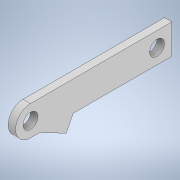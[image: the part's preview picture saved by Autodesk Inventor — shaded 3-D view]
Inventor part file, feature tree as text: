
AUTODESK INVENTOR PART (.ipt)
format: ipt  version: 2021 (Build 250183000, 183)  size: 136,192 bytes
history: native  units: in
note: dims shown in document units (in); Inventor stores cm internally (conversion verified against a paired STEP export)
features: extrude x4, sketch x4, projected_geometry x1
ambient origin geometry x8: Origin, YZ Plane, XZ Plane, XY Plane, X Axis, Y Axis, Z Axis, Center Point
bodies: Solid1 (feature_tree)
feature tree (9):
  extrude  "Extrusion1"  Depth=5.25in
  extrude  "Extrusion2"  Depth=1.0in
  extrude  "Extrusion3"  Depth=0.5in
  extrude  "Extrusion4"  Depth=5.25in
  sketch  "Sketch1"  dims[d0=1.0in d1=5.25in]
  sketch  "Sketch2"  dims[d2=0.25in d3=0.0in d4=1.0in]
  projected_geometry  "Projected Loop1"
  sketch  "Sketch3"  dims[d5=0.5in d6=0.5in]
  sketch  "Sketch4"  dims[d7=4.25in d8=5.25in d9=0.5in d10=0.5in d11=0.5in d12=0.25in d13=0.0in d14=0.25in d15=0.0in d16=0.1886in d19=1.0in d20=0.25in d21=0.0in d22=0.3in]
